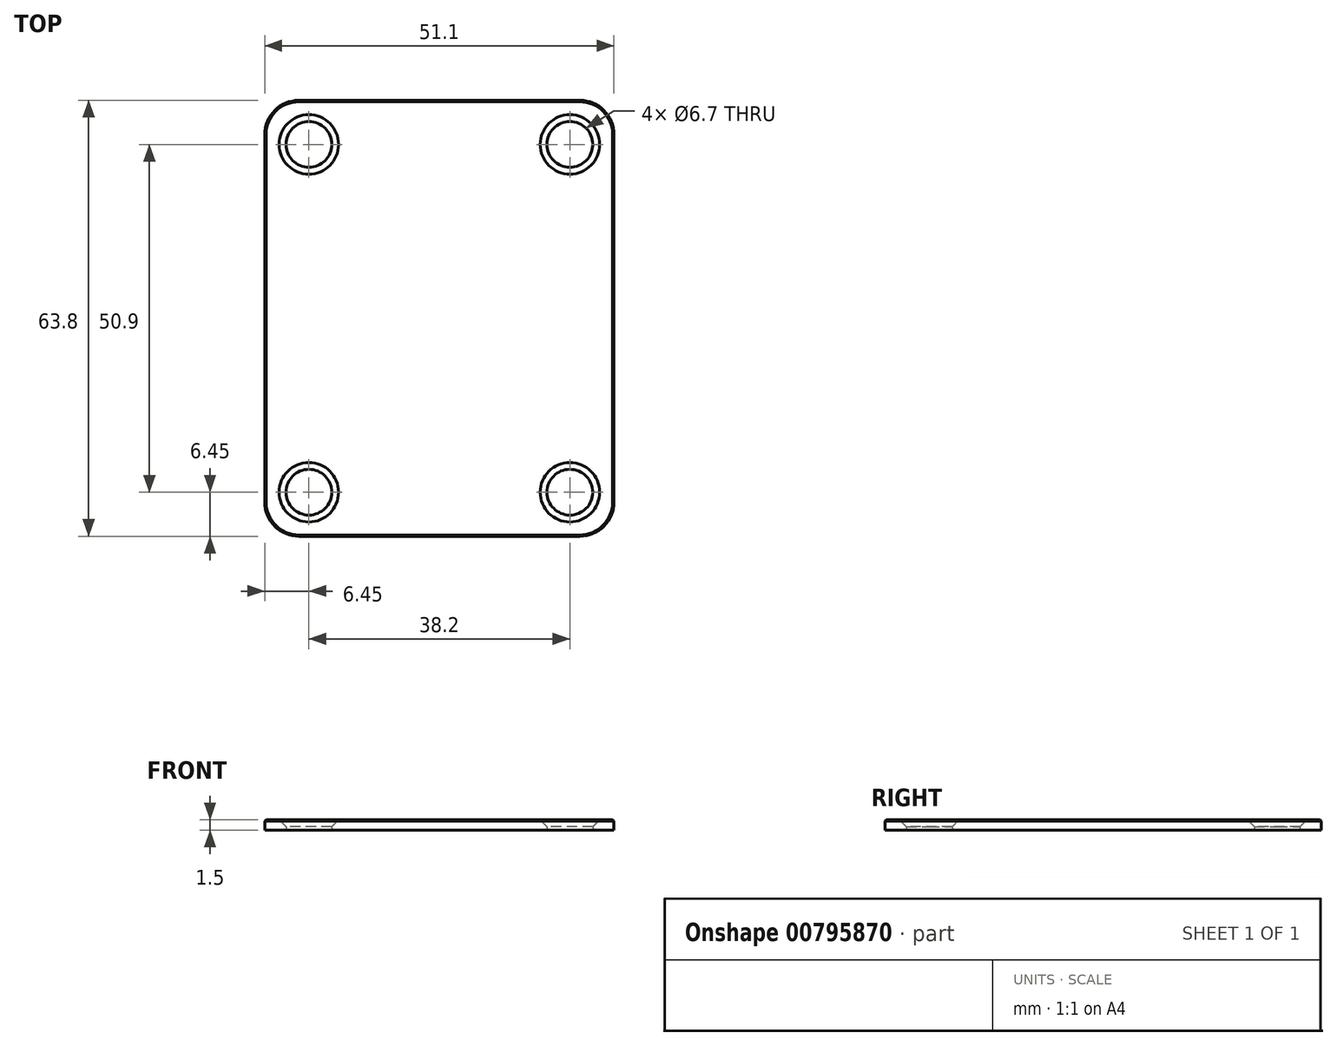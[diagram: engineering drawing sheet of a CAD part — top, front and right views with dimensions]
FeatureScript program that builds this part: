
annotation { "Feature Type Name" : "Feature", "Feature Type Description" : "" }
export const myFeature = defineFeature(function(context is Context, id is Id, definition is map)
    precondition{}
    {
        {
            var Q0;
            Q0=qCreatedBy(makeId("Top.planeOp"),FACE);
            var sketch = newSketch(context, id + "F0", { "sketchPlane" : qUnion([Q0])});
            skLineSegment(sketch, "E0.bottom", {"start": v(-20.55, 31.9) * mm, "end": v(20.55, 31.9) * mm});
            skLineSegment(sketch, "E0.top", {"start": v(-20.55, -31.9) * mm, "end": v(20.55, -31.9) * mm});
            skLineSegment(sketch, "E0.left", {"start": v(-25.55, 26.9) * mm, "end": v(-25.55, -26.9) * mm});
            skLineSegment(sketch, "E0.right", {"start": v(25.55, 26.9) * mm, "end": v(25.55, -26.9) * mm});
            skPoint(sketch, "E1.visualSharp", {"position": v(-25.55, 31.9) * mm});
            skArc(sketch, "E1.filletArc", {"start": v(-20.55, 31.9) * mm, "mid": v(-24.09, 30.44) * mm, "end": v(-25.55, 26.9) * mm});
            skPoint(sketch, "E2.visualSharp", {"position": v(25.55, 31.9) * mm});
            skArc(sketch, "E2.filletArc", {"start": v(25.55, 26.9) * mm, "mid": v(24.09, 30.44) * mm, "end": v(20.55, 31.9) * mm});
            skPoint(sketch, "E3.visualSharp", {"position": v(25.55, -31.9) * mm});
            skArc(sketch, "E3.filletArc", {"start": v(20.55, -31.9) * mm, "mid": v(24.09, -30.44) * mm, "end": v(25.55, -26.9) * mm});
            skPoint(sketch, "E4.visualSharp", {"position": v(-25.55, -31.9) * mm});
            skArc(sketch, "E4.filletArc", {"start": v(-25.55, -26.9) * mm, "mid": v(-24.09, -30.44) * mm, "end": v(-20.55, -31.9) * mm});
            skCircle(sketch, "E5", {"center": v(-19.1, 25.45) * mm, "radius": 3.35 * mm});
            skCircle(sketch, "E6.0.1.0", {"center": v(-19.1, -25.45) * mm, "radius": 3.35 * mm});
            skCircle(sketch, "E6.1.0.0", {"center": v(19.1, 25.45) * mm, "radius": 3.35 * mm});
            skCircle(sketch, "E6.1.1.0", {"center": v(19.1, -25.45) * mm, "radius": 3.35 * mm});
            skLineSegment(sketch, "E6.direction1", {"start": v(-19.1, 25.45) * mm, "end": v(19.1, 25.45) * mm, "construction": true});
            skLineSegment(sketch, "E6.direction2", {"start": v(-19.1, 25.45) * mm, "end": v(-19.1, -25.45) * mm, "construction": true});
            skSolve(sketch);
        }
        {
            var Q0;
            Q0 = qSketchRegion(id + "F0", true);
            extrude(context, id + "F1", {"entities" : qUnion([Q0]), "depth" : 1.5 * mm, "offsetDistance" : 25 * mm});
        }
        {
            var Q0;
            Q0=makeQuery(id+"F1.opExtrude","CAP_EDGE",EDGE,{"disambiguationData":[OSD([sQuery(id+"F0.wireOp",EDGE,"E5")])],"isStart":false});
            var Q1;
            Q1=makeQuery(id+"F1.opExtrude","CAP_EDGE",EDGE,{"disambiguationData":[OSD([sQuery(id+"F0.wireOp",EDGE,"E6.1.0.0")])],"isStart":false});
            var Q2;
            Q2=makeQuery(id+"F1.opExtrude","CAP_EDGE",EDGE,{"disambiguationData":[OSD([sQuery(id+"F0.wireOp",EDGE,"E6.1.1.0")])],"isStart":false});
            var Q3;
            Q3=makeQuery(id+"F1.opExtrude","CAP_EDGE",EDGE,{"disambiguationData":[OSD([sQuery(id+"F0.wireOp",EDGE,"E6.0.1.0")])],"isStart":false});
            chamfer(context, id + "F2", {"entities" : qUnion([Q0, Q1, Q2, Q3]), "width" : 1 * mm, "tangentPropagation" : true});
        }
        {
            var Q0;
            Q0=makeQuery(id+"F1.opExtrude","CAP_EDGE",EDGE,{"disambiguationData":[OSD([sQuery(id+"F0.wireOp",EDGE,"E1.filletArc")])],"isStart":false});
            var Q1;
            Q1=makeQuery(id+"F1.opExtrude","CAP_EDGE",EDGE,{"disambiguationData":[OSD([sQuery(id+"F0.wireOp",EDGE,"E0.left")])],"isStart":false});
            var Q2;
            Q2=makeQuery(id+"F1.opExtrude","CAP_EDGE",EDGE,{"disambiguationData":[OSD([sQuery(id+"F0.wireOp",EDGE,"E4.filletArc")])],"isStart":false});
            var Q3;
            Q3=makeQuery(id+"F1.opExtrude","CAP_EDGE",EDGE,{"disambiguationData":[OSD([sQuery(id+"F0.wireOp",EDGE,"E0.bottom")])],"isStart":false});
            var Q4;
            Q4=makeQuery(id+"F1.opExtrude","CAP_EDGE",EDGE,{"disambiguationData":[OSD([sQuery(id+"F0.wireOp",EDGE,"E2.filletArc")])],"isStart":false});
            var Q5;
            Q5=makeQuery(id+"F1.opExtrude","CAP_EDGE",EDGE,{"disambiguationData":[OSD([sQuery(id+"F0.wireOp",EDGE,"E0.right")])],"isStart":false});
            var Q6;
            Q6=makeQuery(id+"F1.opExtrude","CAP_EDGE",EDGE,{"disambiguationData":[OSD([sQuery(id+"F0.wireOp",EDGE,"E3.filletArc")])],"isStart":false});
            var Q7;
            Q7=makeQuery(id+"F1.opExtrude","CAP_EDGE",EDGE,{"disambiguationData":[OSD([sQuery(id+"F0.wireOp",EDGE,"E0.top")])],"isStart":false});
            chamfer(context, id + "F3", {"entities" : qUnion([Q0, Q1, Q2, Q3, Q4, Q5, Q6, Q7]), "width" : 0.2 * mm, "tangentPropagation" : true});
        }
    });
